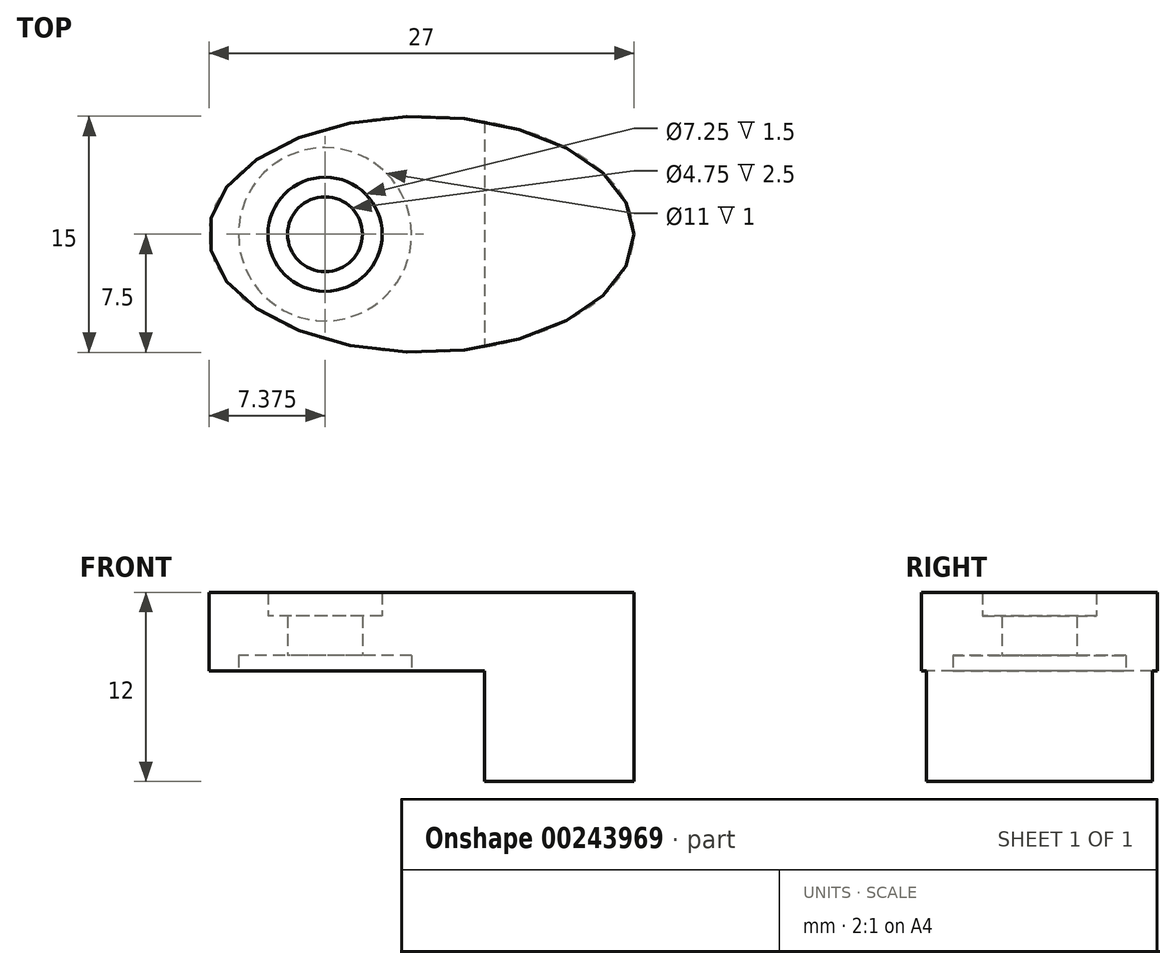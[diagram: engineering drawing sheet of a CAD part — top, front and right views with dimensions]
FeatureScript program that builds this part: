
annotation { "Feature Type Name" : "Feature", "Feature Type Description" : "" }
export const myFeature = defineFeature(function(context is Context, id is Id, definition is map)
    precondition{}
    {
        {
            var Q0;
            Q0=qCreatedBy(makeId("Top.planeOp"),FACE);
            var sketch = newSketch(context, id + "F0", { "sketchPlane" : qUnion([Q0])});
            skEllipse(sketch, "E0", {"center": v(0, 0) * mm, "majorRadius": 13.5 * mm, "minorRadius": 7.5 * mm, "majorAxis": v(1, 0)});
            skCircle(sketch, "E1", {"center": v(-6.12, 0) * mm, "radius": 2.38 * mm});
            skLineSegment(sketch, "E2", {"start": v(-8.5, 0) * mm, "end": v(-13.5, 0) * mm});
            skLineSegment(sketch, "E3", {"start": v(-13.5, 0) * mm, "end": v(-8.5, 0) * mm, "construction": true});
            skCircle(sketch, "E4", {"center": v(-6.12, 0) * mm, "radius": 3.62 * mm});
            skLineSegment(sketch, "E5", {"start": v(4, 7.16) * mm, "end": v(4, -7.16) * mm});
            skLineSegment(sketch, "E6", {"start": v(4, 0) * mm, "end": v(13.5, 0) * mm, "construction": true});
            skCircle(sketch, "E7", {"center": v(-6.12, 0) * mm, "radius": 5.5 * mm});
            skSolve(sketch);
        }
        {
            var Q0;
            Q0=makeQuery(id+"F0.imprint","IMPRINT",FACE,{"disambiguationData":[TD([[makeQuery(id+"F0.imprint","IMPRINT",EDGE,{"derivedFrom":sQuery(id+"F0.wireOp",EDGE,"E4")}),-1.0]])]});
            var Q1;
            {var subQ0=sQuery(id+"F0.wireOp",EDGE,"E5");Q1=makeQuery(id+"F0.imprint","IMPRINT",FACE,{"disambiguationData":[TD([[makeQuery(id+"F0.imprint","IMPRINT",EDGE,{"derivedFrom":subQ0}),1.0]])]});}
            var Q2;
            {var subQ2=sQuery(id+"F0.wireOp",EDGE,"E5");Q2=makeQuery(id+"F0.imprint","IMPRINT",FACE,{"disambiguationData":[TD([[makeQuery(id+"F0.imprint","IMPRINT",EDGE,{"derivedFrom":subQ2}),-1.0]])]});}
            extrude(context, id + "F1", {"entities" : qUnion([Q0, Q1, Q2]), "depth" : 5 * mm});
        }
        {
            var Q0;
            Q0=makeQuery(id+"F0.imprint","IMPRINT",FACE,{"disambiguationData":[TD([[makeQuery(id+"F0.imprint","IMPRINT",EDGE,{"derivedFrom":sQuery(id+"F0.wireOp",EDGE,"E1")}),-1.0]])]});
            extrude(context, id + "F2", {"entities" : qUnion([Q0]), "operationType" : NewBodyOperationType.ADD, "depth" : 3.5 * mm});
        }
        {
            var Q0;
            {var subQ0=sQuery(id+"F0.wireOp",EDGE,"E5");Q0=makeQuery(id+"F0.imprint","IMPRINT",FACE,{"disambiguationData":[TD([[makeQuery(id+"F0.imprint","IMPRINT",EDGE,{"derivedFrom":subQ0}),1.0]])]});}
            extrude(context, id + "F3", {"entities" : qUnion([Q0]), "operationType" : NewBodyOperationType.ADD, "oppositeDirection" : true, "depth" : 7 * mm});
        }
        {
            var Q0;
            Q0=makeQuery(id+"F0.imprint","IMPRINT",FACE,{"disambiguationData":[TD([[makeQuery(id+"F0.imprint","IMPRINT",EDGE,{"derivedFrom":sQuery(id+"F0.wireOp",EDGE,"E4")}),-1.0]])]});
            var Q1;
            Q1=makeQuery(id+"F0.imprint","IMPRINT",FACE,{"disambiguationData":[TD([[makeQuery(id+"F0.imprint","IMPRINT",EDGE,{"derivedFrom":sQuery(id+"F0.wireOp",EDGE,"E1")}),-1.0]])]});
            extrude(context, id + "F4", {"entities" : qUnion([Q0, Q1]), "operationType" : NewBodyOperationType.REMOVE, "depth" : 1 * mm});
        }
    });
